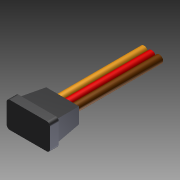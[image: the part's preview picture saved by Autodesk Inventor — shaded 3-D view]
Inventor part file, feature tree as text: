
AUTODESK INVENTOR PART (.ipt)
format: ipt  version: 2015 (Build 190159000, 159)  size: 105,984 bytes
history: native  units: in
note: dims shown in document units (in); Inventor stores cm internally (conversion verified against a paired STEP export)
features: other x4, imported_body x4, fillet x1
ambient origin geometry x8: Origin, YZ Plane, XZ Plane, XY Plane, X Axis, Y Axis, Z Axis, Center Point
bodies: Body1 (feature_tree), Body2 (feature_tree), Body3 (feature_tree), Body4 (feature_tree)
feature tree (9):
  fillet  "Fillet1"  [1 undecoded]
  other  "TOWER PRO MG-995, ANALOG SERVO, CONNECTOR.ipt1"
  other  "POSITIVE"
  other  "SIGNAL"
  other  "NEGATIVE"
  imported_body  "Base1"
  imported_body  "Base2"
  imported_body  "Base3"
  imported_body  "Base4"
note: 1 required parameter value undecoded (feature->parameter linkage not recoverable at this tier; creation-order binding heuristic only, values carry confidence <= 0.55)
